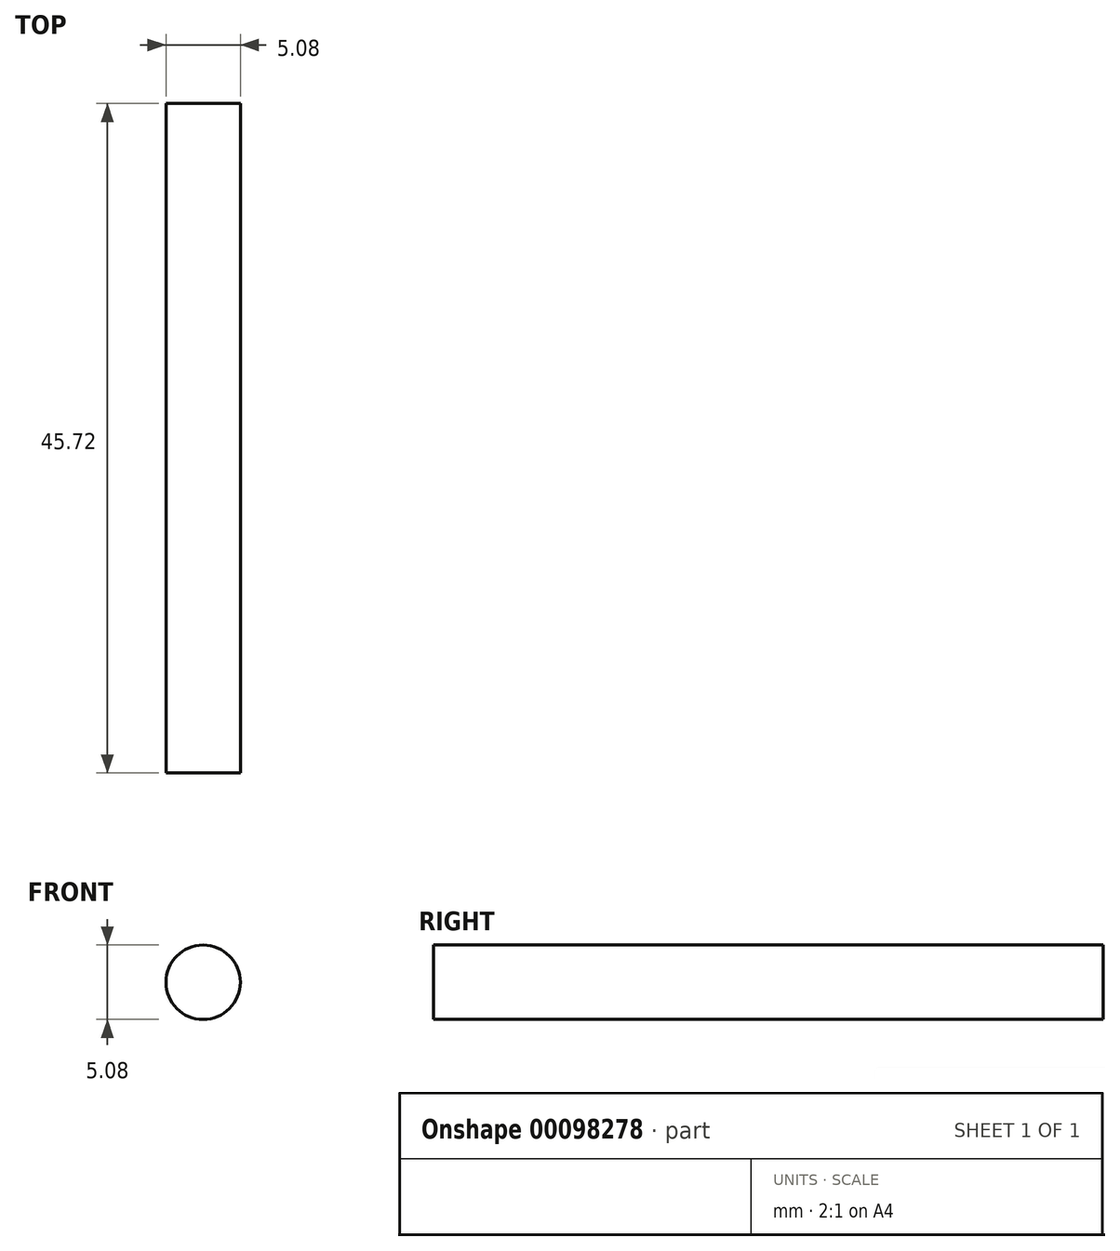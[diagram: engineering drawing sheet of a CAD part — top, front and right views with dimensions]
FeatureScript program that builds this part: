
annotation { "Feature Type Name" : "Feature", "Feature Type Description" : "" }
export const myFeature = defineFeature(function(context is Context, id is Id, definition is map)
    precondition{}
    {
        {
            var Q0;
            Q0=qCreatedBy(makeId("Front.planeOp"),FACE);
            var sketch = newSketch(context, id + "F0", { "sketchPlane" : qUnion([Q0])});
            skCircle(sketch, "E0", {"center": v(0, 0) * mm, "radius": 2.54 * mm});
            skSolve(sketch);
        }
        {
            var Q0;
            Q0=makeQuery(id+"F0.imprint","IMPRINT",FACE,{"disambiguationData":[TD([[makeQuery(id+"F0.imprint","IMPRINT",EDGE,{"derivedFrom":sQuery(id+"F0.wireOp",EDGE,"E0")}),1.0]])]});
            extrude(context, id + "F1", {"entities" : qUnion([Q0]), "depth" : 45.72 * mm});
        }
    });
